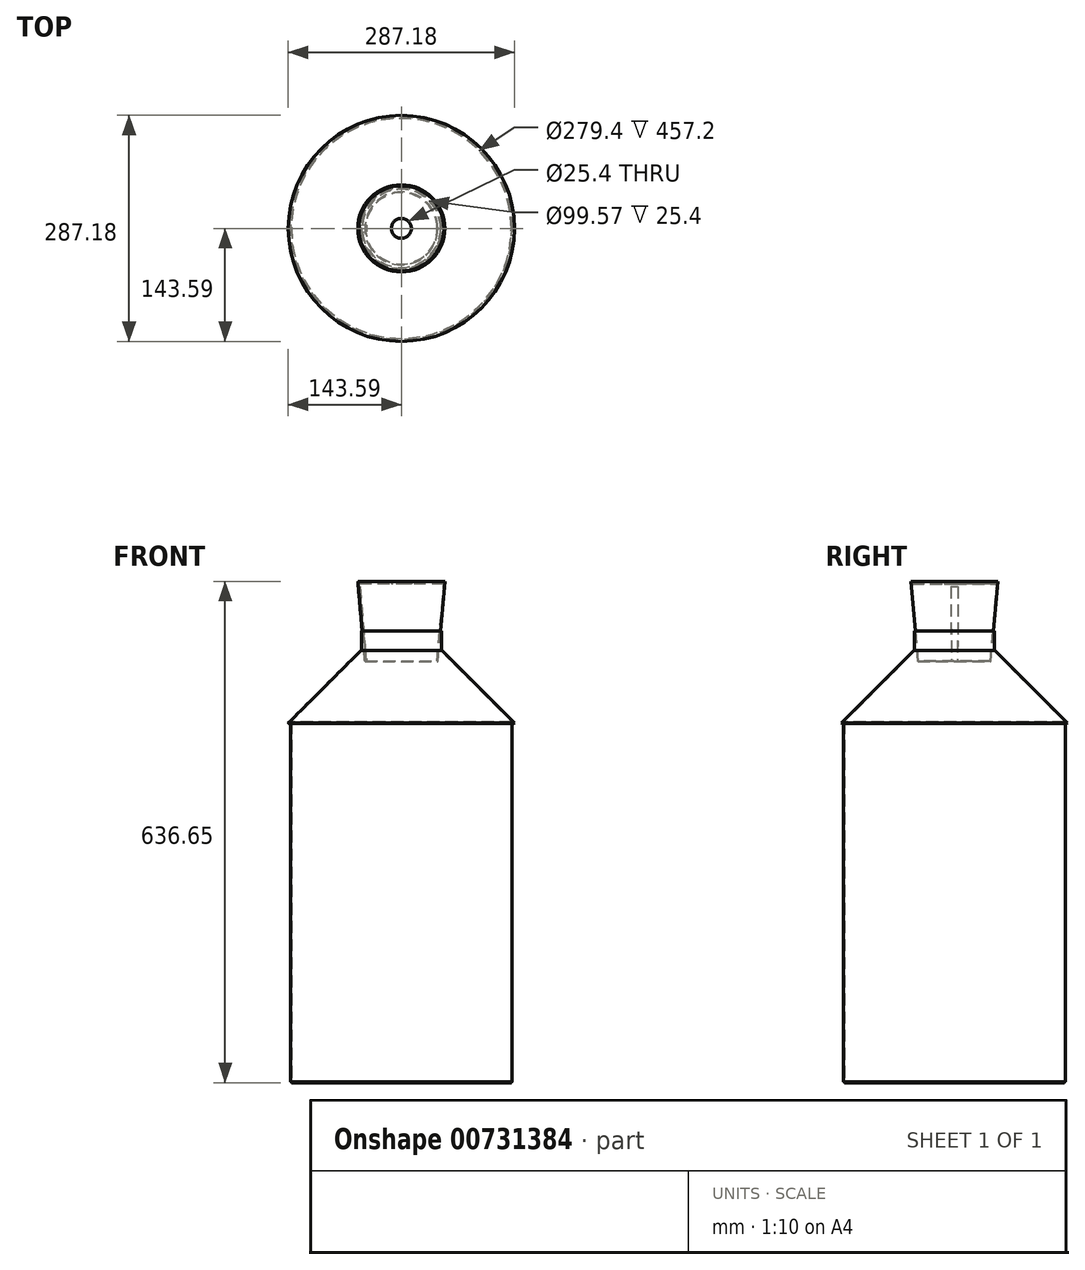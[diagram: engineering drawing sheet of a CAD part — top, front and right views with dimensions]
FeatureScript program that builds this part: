
annotation { "Feature Type Name" : "Feature", "Feature Type Description" : "" }
export const myFeature = defineFeature(function(context is Context, id is Id, definition is map)
    precondition{}
    {
        {
            var Q0;
            Q0=qCreatedBy(makeId("Top.planeOp"),FACE);
            var sketch = newSketch(context, id + "F0", { "sketchPlane" : qUnion([Q0])});
            skCircle(sketch, "E0", {"center": v(0, 0) * mm, "radius": 139.7 * mm});
            skSolve(sketch);
        }
        {
            var Q0;
            Q0=makeQuery(id+"F0.imprint","IMPRINT",FACE,{"disambiguationData":[TD([[makeQuery(id+"F0.imprint","IMPRINT",EDGE,{"derivedFrom":sQuery(id+"F0.wireOp",EDGE,"E0")}),1.0]])]});
            extrude(context, id + "F1", {"entities" : qUnion([Q0]), "oppositeDirection" : true, "depth" : 1.02 * mm, "offsetDistance" : 25.4 * mm});
        }
        {
            var Q0;
            Q0=makeQuery(id+"F1.opExtrude","CAP_FACE",FACE,{"disambiguationData":[OSD([sQuery(id+"F0.wireOp",EDGE,"E0")])],"isStart":true});
            var sketch = newSketch(context, id + "F2", { "sketchPlane" : qUnion([Q0])});
            skCircle(sketch, "E1.0", {"center": v(0, 0) * mm, "radius": 139.7 * mm});
            skCircle(sketch, "E2.0", {"center": v(0, 0) * mm, "radius": 140.72 * mm});
            skSolve(sketch);
        }
        {
            var Q0;
            Q0 = qSketchRegion(id + "F2", true);
            extrude(context, id + "F3", {"entities" : qUnion([Q0]), "depth" : 457.2 * mm, "offsetDistance" : 25.4 * mm});
        }
        {
            var Q0;
            Q0=qCreatedBy(makeId("Front.planeOp"),FACE);
            var sketch = newSketch(context, id + "F4", { "sketchPlane" : qUnion([Q0])});
            skLineSegment(sketch, "E3", {"start": v(-142.88, 455.04) * mm, "end": v(-50.8, 547.12) * mm});
            skLineSegment(sketch, "E4", {"start": v(0, 0) * mm, "end": v(0, 593.13) * mm, "construction": true});
            skPoint(sketch, "E5", {"position": v(-140.72, 457.2) * mm});
            skLineSegment(sketch, "E6.0", {"start": v(-143.6, 455.76) * mm, "end": v(-51.52, 547.83) * mm});
            skLineSegment(sketch, "E7", {"start": v(-143.6, 455.76) * mm, "end": v(-142.87, 455.04) * mm});
            skLineSegment(sketch, "E8", {"start": v(-51.52, 547.83) * mm, "end": v(-50.8, 547.12) * mm});
            skSolve(sketch);
        }
        {
            var Q0;
            Q0=makeQuery(id+"F4.imprint","IMPRINT",FACE,{"disambiguationData":[TD([[makeQuery(id+"F4.imprint","IMPRINT",EDGE,{"derivedFrom":sQuery(id+"F4.wireOp",EDGE,"E3")}),1.0]])]});
            var Q1;
            Q1=sQuery(id+"F4.wireOp",EDGE,"E4");
            revolve(context, id + "F5", {"surfaceOperationType" : NewSurfaceOperationType.NEW, "entities" : qUnion([Q0]), "axis" : qUnion([Q1]), "revolveType" : RevolveType.FULL});
        }
        {
            var Q0;
            Q0=qCreatedBy(makeId("Front.planeOp"),FACE);
            var sketch = newSketch(context, id + "F6", { "sketchPlane" : qUnion([Q0])});
            skLineSegment(sketch, "E9", {"start": v(0, 0) * mm, "end": v(0, 630.96) * mm, "construction": true});
            skLineSegment(sketch, "E10.bottom", {"start": v(-50.8, 572.52) * mm, "end": v(-49.78, 572.52) * mm});
            skLineSegment(sketch, "E10.top", {"start": v(-50.8, 547.12) * mm, "end": v(-49.78, 547.12) * mm});
            skLineSegment(sketch, "E10.left", {"start": v(-50.8, 572.52) * mm, "end": v(-50.8, 547.12) * mm});
            skLineSegment(sketch, "E10.right", {"start": v(-49.78, 572.52) * mm, "end": v(-49.78, 547.12) * mm});
            skPoint(sketch, "E11", {"position": v(-50.8, 547.12) * mm});
            skSolve(sketch);
        }
        {
            var Q0;
            Q0=makeQuery(id+"F6.imprint","IMPRINT",FACE,{"disambiguationData":[TD([[makeQuery(id+"F6.imprint","IMPRINT",EDGE,{"derivedFrom":sQuery(id+"F6.wireOp",EDGE,"E10.bottom")}),-1.0]])]});
            var Q1;
            Q1=sQuery(id+"F6.wireOp",EDGE,"E9");
            revolve(context, id + "F7", {"surfaceOperationType" : NewSurfaceOperationType.NEW, "entities" : qUnion([Q0]), "axis" : qUnion([Q1]), "revolveType" : RevolveType.FULL});
        }
        {
            var Q0;
            Q0=qCreatedBy(makeId("Front.planeOp"),FACE);
            var sketch = newSketch(context, id + "F8", { "sketchPlane" : qUnion([Q0])});
            skLineSegment(sketch, "E12", {"start": v(-55.3, 635.54) * mm, "end": v(-46.44, 534.33) * mm});
            skLineSegment(sketch, "E13", {"start": v(0, 0) * mm, "end": v(0, 635.63) * mm, "construction": true});
            skLineSegment(sketch, "E14.0", {"start": v(-54.29, 635.63) * mm, "end": v(-45.43, 534.42) * mm});
            skLineSegment(sketch, "E15", {"start": v(-46.44, 534.33) * mm, "end": v(-45.43, 534.42) * mm});
            skLineSegment(sketch, "E16", {"start": v(-55.3, 635.54) * mm, "end": v(-54.29, 635.63) * mm});
            skSolve(sketch);
        }
        {
            var Q0;
            Q0 = qSketchRegion(id + "F8", true);
            var Q1;
            Q1=sQuery(id+"F8.wireOp",EDGE,"E13");
            revolve(context, id + "F9", {"surfaceOperationType" : NewSurfaceOperationType.NEW, "entities" : qUnion([Q0]), "axis" : qUnion([Q1]), "revolveType" : RevolveType.FULL});
        }
        {
            var Q0;
            Q0=sQuery(id+"F8.wireOp",VERTEX,"E13.end");
            var Q1;
            Q1=qCreatedBy(makeId("Top.planeOp"),FACE);
            cPlane(context, id + "F10", {"entities" : qUnion([Q0, Q1]), "cplaneType" : CPlaneType.PLANE_POINT, "offset" : 25.4 * mm, "width" : 152.4 * mm, "height" : 152.4 * mm});
        }
        {
            var Q0;
            Q0=qCreatedBy(id+"F10.planeOp",FACE);
            cPlane(context, id + "F11", {"entities" : qUnion([Q0]), "cplaneType" : CPlaneType.OFFSET, "offset" : 3.17 * mm, "oppositeDirection" : true, "width" : 152.4 * mm, "height" : 152.4 * mm});
        }
        {
            var Q0;
            Q0=qCreatedBy(id+"F11.planeOp",FACE);
            var sketch = newSketch(context, id + "F12", { "sketchPlane" : qUnion([Q0])});
            skCircle(sketch, "E17", {"center": v(0, 0) * mm, "radius": 12.7 * mm});
            skCircle(sketch, "E18", {"center": v(0, 0) * mm, "radius": 54 * mm});
            skSolve(sketch);
        }
        {
            var Q0;
            Q0 = qSketchRegion(id + "F12", true);
            extrude(context, id + "F13", {"entities" : qUnion([Q0]), "depth" : 1.02 * mm, "offsetDistance" : 25.4 * mm});
        }
        {
            var Q0;
            Q0=qCreatedBy(makeId("Front.planeOp"),FACE);
            var sketch = newSketch(context, id + "F14", { "sketchPlane" : qUnion([Q0])});
            skLineSegment(sketch, "E19.0", {"start": v(-53.73, 629.3) * mm, "end": v(-45.43, 534.42) * mm});
            skLineSegment(sketch, "E20.0", {"start": v(-52.72, 629.4) * mm, "end": v(-44.42, 534.5) * mm});
            skLineSegment(sketch, "E21", {"start": v(-44.42, 534.5) * mm, "end": v(-45.43, 534.42) * mm});
            skLineSegment(sketch, "E22", {"start": v(-53.73, 629.3) * mm, "end": v(-52.72, 629.4) * mm});
            skPoint(sketch, "E23.orphan", {"position": v(-54.29, 635.63) * mm});
            skLineSegment(sketch, "E24", {"start": v(0, 0) * mm, "end": v(0, 695.73) * mm, "construction": true});
            skSolve(sketch);
        }
        {
            var Q0;
            Q0 = qSketchRegion(id + "F14", true);
            var Q1;
            Q1=sQuery(id+"F14.wireOp",EDGE,"E24");
            revolve(context, id + "F15", {"surfaceOperationType" : NewSurfaceOperationType.NEW, "entities" : qUnion([Q0]), "axis" : qUnion([Q1]), "revolveType" : RevolveType.SYMMETRIC, "angle" : 10 * degree});
        }
    });
